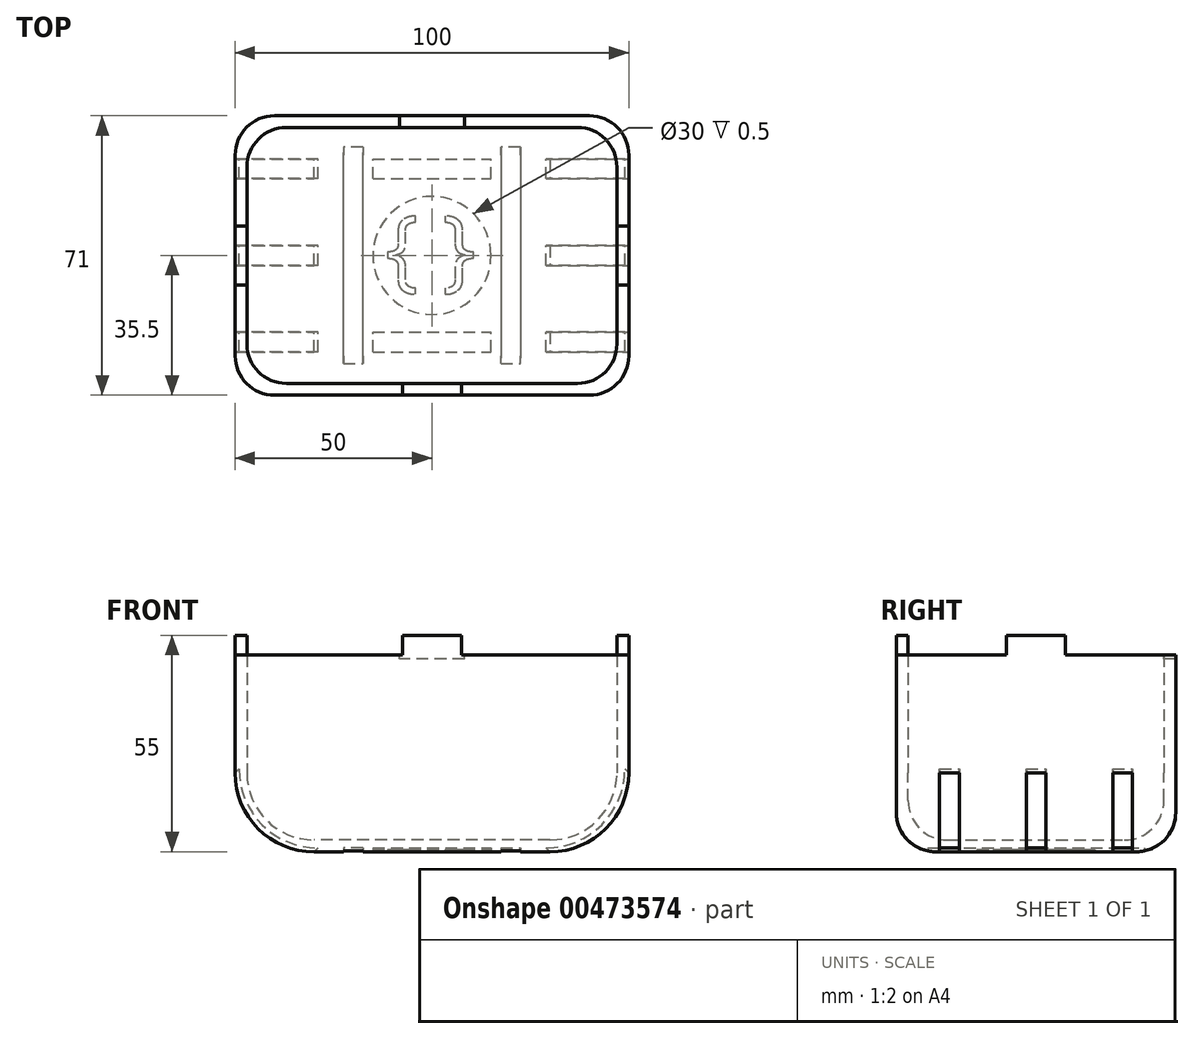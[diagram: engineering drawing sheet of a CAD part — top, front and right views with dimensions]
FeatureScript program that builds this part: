
annotation { "Feature Type Name" : "Feature", "Feature Type Description" : "" }
export const myFeature = defineFeature(function(context is Context, id is Id, definition is map)
    precondition{}
    {
        {
            var Q0;
            Q0=qCreatedBy(makeId("Top.planeOp"),FACE);
            var sketch = newSketch(context, id + "F0", { "sketchPlane" : qUnion([Q0])});
            skLineSegment(sketch, "E0.bottom", {"start": v(42.5, 28) * mm, "end": v(-42.5, 28) * mm});
            skLineSegment(sketch, "E0.top", {"start": v(42.5, -28) * mm, "end": v(-42.5, -28) * mm});
            skLineSegment(sketch, "E0.left", {"start": v(42.5, 28) * mm, "end": v(42.5, -28) * mm});
            skLineSegment(sketch, "E0.right", {"start": v(-42.5, 28) * mm, "end": v(-42.5, -28) * mm});
            skPoint(sketch, "E0.middle", {"position": v(0, 0) * mm});
            skLineSegment(sketch, "E1.bottom", {"start": v(50, 35.5) * mm, "end": v(-50, 35.5) * mm});
            skLineSegment(sketch, "E1.top", {"start": v(50, -35.5) * mm, "end": v(-50, -35.5) * mm});
            skLineSegment(sketch, "E1.left", {"start": v(50, 35.5) * mm, "end": v(50, -35.5) * mm});
            skLineSegment(sketch, "E1.right", {"start": v(-50, 35.5) * mm, "end": v(-50, -35.5) * mm});
            skSolve(sketch);
        }
        {
            var Q0;
            Q0=makeQuery(id+"F0.imprint","IMPRINT",FACE,{"disambiguationData":[TD([[makeQuery(id+"F0.imprint","IMPRINT",EDGE,{"derivedFrom":sQuery(id+"F0.wireOp",EDGE,"E0.bottom")}),-1.0]])]});
            var Q1;
            Q1=makeQuery(id+"F0.imprint","IMPRINT",FACE,{"disambiguationData":[TD([[makeQuery(id+"F0.imprint","IMPRINT",EDGE,{"derivedFrom":sQuery(id+"F0.wireOp",EDGE,"E0.bottom")}),1.0]])]});
            extrude(context, id + "F1", {"entities" : qUnion([Q0, Q1]), "depth" : 55 * mm});
        }
        {
            var Q0;
            Q0=makeQuery(id+"F1.opExtrude","CAP_EDGE",EDGE,{"disambiguationData":[OSD([sQuery(id+"F0.wireOp",EDGE,"E1.right")])],"isStart":true});
            var Q1;
            Q1=makeQuery(id+"F1.opExtrude","CAP_EDGE",EDGE,{"disambiguationData":[OSD([sQuery(id+"F0.wireOp",EDGE,"E1.left")])],"isStart":true});
            fillet(context, id + "F2", {"entities" : qUnion([Q0, Q1]), "radius" : 20 * mm, "tangentPropagation" : true, "allowEdgeOverflow" : false});
        }
        {
            var Q0;
            Q0=makeQuery(id+"F1.opExtrude","CAP_FACE",FACE,{"disambiguationData":[OSD([sQuery(id+"F0.wireOp",EDGE,"E1.bottom"),sQuery(id+"F0.wireOp",EDGE,"E1.top"),sQuery(id+"F0.wireOp",EDGE,"E1.left"),sQuery(id+"F0.wireOp",EDGE,"E1.right")])],"isStart":false});
            shell(context, id + "F3", {"entities" : qUnion([Q0]), "thickness" : 3 * mm});
        }
        {
            var Q0;
            Q0=makeQuery(id+"F1.opExtrude","SWEPT_FACE",FACE,{"disambiguationData":[OSD([sQuery(id+"F0.wireOp",EDGE,"E1.bottom")])]});
            var sketch = newSketch(context, id + "F4", { "sketchPlane" : qUnion([Q0])});
            skLineSegment(sketch, "E2.bottom", {"start": v(-50, 55) * mm, "end": v(50, 55) * mm});
            skLineSegment(sketch, "E2.top", {"start": v(-50, 0) * mm, "end": v(50, 0) * mm});
            skLineSegment(sketch, "E2.left", {"start": v(-50, 55) * mm, "end": v(-50, 0) * mm});
            skLineSegment(sketch, "E2.right", {"start": v(50, 55) * mm, "end": v(50, 0) * mm});
            skPoint(sketch, "E3", {"position": v(0, 27.5) * mm});
            skPoint(sketch, "E3.positionSnap0", {"position": v(-50, 27.5) * mm});
            skLineSegment(sketch, "E4.bottom", {"start": v(49, 54) * mm, "end": v(-49, 54) * mm});
            skLineSegment(sketch, "E4.top", {"start": v(29, 1) * mm, "end": v(-29, 1) * mm});
            skLineSegment(sketch, "E4.left", {"start": v(49, 54) * mm, "end": v(49, 21) * mm});
            skLineSegment(sketch, "E4.right", {"start": v(-49, 54) * mm, "end": v(-49, 21) * mm});
            skPoint(sketch, "E5.visualSharp", {"position": v(49, 1) * mm});
            skArc(sketch, "E5.filletArc", {"start": v(29, 1) * mm, "mid": v(43.14, 6.86) * mm, "end": v(49, 21) * mm});
            skPoint(sketch, "E6.visualSharp", {"position": v(-49, 1) * mm});
            skArc(sketch, "E6.filletArc", {"start": v(-49, 21) * mm, "mid": v(-43.14, 6.86) * mm, "end": v(-29, 1) * mm});
            skLineSegment(sketch, "E7", {"start": v(-29, 1) * mm, "end": v(-30, 0) * mm});
            skLineSegment(sketch, "E8", {"start": v(29, 1) * mm, "end": v(30, 0) * mm});
            skLineSegment(sketch, "E9", {"start": v(49, 21) * mm, "end": v(50, 20) * mm});
            skLineSegment(sketch, "E10", {"start": v(-49, 21) * mm, "end": v(-50, 20) * mm});
            skSolve(sketch);
        }
        {
            var Q0;
            Q0=makeQuery(id+"F4.imprint","IMPRINT",FACE,{"disambiguationData":[TD([[makeQuery(id+"F4.imprint","IMPRINT",EDGE,{"derivedFrom":sQuery(id+"F4.wireOp",EDGE,"E6.filletArc")}),-1.0]])]});
            var Q1;
            Q1=makeQuery(id+"F4.imprint","IMPRINT",FACE,{"disambiguationData":[TD([[makeQuery(id+"F4.imprint","IMPRINT",EDGE,{"derivedFrom":sQuery(id+"F4.wireOp",EDGE,"E5.filletArc")}),-1.0]])]});
            extrude(context, id + "F5", {"entities" : qUnion([Q0, Q1]), "operationType" : NewBodyOperationType.REMOVE, "oppositeDirection" : true, "depth" : 60 * mm});
        }
        {
            var Q0;
            Q0=makeQuery(id+"F4.imprint","IMPRINT",FACE,{"disambiguationData":[TD([[makeQuery(id+"F4.imprint","IMPRINT",EDGE,{"derivedFrom":sQuery(id+"F4.wireOp",EDGE,"E6.filletArc")}),-1.0]])]});
            var Q1;
            Q1=makeQuery(id+"F4.imprint","IMPRINT",FACE,{"disambiguationData":[TD([[makeQuery(id+"F4.imprint","IMPRINT",EDGE,{"derivedFrom":sQuery(id+"F4.wireOp",EDGE,"E5.filletArc")}),-1.0]])]});
            extrude(context, id + "F6", {"entities" : qUnion([Q0, Q1]), "operationType" : NewBodyOperationType.ADD, "oppositeDirection" : true, "depth" : 55 * mm});
        }
        {
            var Q0;
            Q0=makeQuery(id+"F4.imprint","IMPRINT",FACE,{"disambiguationData":[TD([[makeQuery(id+"F4.imprint","IMPRINT",EDGE,{"derivedFrom":sQuery(id+"F4.wireOp",EDGE,"E6.filletArc")}),-1.0]])]});
            var Q1;
            Q1=makeQuery(id+"F4.imprint","IMPRINT",FACE,{"disambiguationData":[TD([[makeQuery(id+"F4.imprint","IMPRINT",EDGE,{"derivedFrom":sQuery(id+"F4.wireOp",EDGE,"E5.filletArc")}),-1.0]])]});
            extrude(context, id + "F7", {"entities" : qUnion([Q0, Q1]), "operationType" : NewBodyOperationType.REMOVE, "oppositeDirection" : true, "depth" : 38 * mm});
        }
        {
            var Q0;
            Q0=makeQuery(id+"F4.imprint","IMPRINT",FACE,{"disambiguationData":[TD([[makeQuery(id+"F4.imprint","IMPRINT",EDGE,{"derivedFrom":sQuery(id+"F4.wireOp",EDGE,"E6.filletArc")}),-1.0]])]});
            var Q1;
            Q1=makeQuery(id+"F4.imprint","IMPRINT",FACE,{"disambiguationData":[TD([[makeQuery(id+"F4.imprint","IMPRINT",EDGE,{"derivedFrom":sQuery(id+"F4.wireOp",EDGE,"E5.filletArc")}),-1.0]])]});
            extrude(context, id + "F8", {"entities" : qUnion([Q0, Q1]), "operationType" : NewBodyOperationType.ADD, "oppositeDirection" : true, "depth" : 33 * mm});
        }
        {
            var Q0;
            Q0=makeQuery(id+"F4.imprint","IMPRINT",FACE,{"disambiguationData":[TD([[makeQuery(id+"F4.imprint","IMPRINT",EDGE,{"derivedFrom":sQuery(id+"F4.wireOp",EDGE,"E6.filletArc")}),-1.0]])]});
            var Q1;
            Q1=makeQuery(id+"F4.imprint","IMPRINT",FACE,{"disambiguationData":[TD([[makeQuery(id+"F4.imprint","IMPRINT",EDGE,{"derivedFrom":sQuery(id+"F4.wireOp",EDGE,"E5.filletArc")}),-1.0]])]});
            extrude(context, id + "F9", {"entities" : qUnion([Q0, Q1]), "operationType" : NewBodyOperationType.REMOVE, "oppositeDirection" : true, "depth" : 16 * mm});
        }
        {
            var Q0;
            Q0=makeQuery(id+"F4.imprint","IMPRINT",FACE,{"disambiguationData":[TD([[makeQuery(id+"F4.imprint","IMPRINT",EDGE,{"derivedFrom":sQuery(id+"F4.wireOp",EDGE,"E6.filletArc")}),-1.0]])]});
            var Q1;
            Q1=makeQuery(id+"F4.imprint","IMPRINT",FACE,{"disambiguationData":[TD([[makeQuery(id+"F4.imprint","IMPRINT",EDGE,{"derivedFrom":sQuery(id+"F4.wireOp",EDGE,"E5.filletArc")}),-1.0]])]});
            extrude(context, id + "F10", {"entities" : qUnion([Q0, Q1]), "operationType" : NewBodyOperationType.ADD, "oppositeDirection" : true, "depth" : 11 * mm});
        }
        {
            var Q0;
            Q0=makeQuery(id+"F1.opExtrude","CAP_FACE",FACE,{"disambiguationData":[OSD([sQuery(id+"F0.wireOp",EDGE,"E1.bottom"),sQuery(id+"F0.wireOp",EDGE,"E1.top"),sQuery(id+"F0.wireOp",EDGE,"E1.left"),sQuery(id+"F0.wireOp",EDGE,"E1.right")])],"isStart":true});
            var sketch = newSketch(context, id + "F11", { "sketchPlane" : qUnion([Q0])});
            skLineSegment(sketch, "E11.bottom", {"start": v(30, 35.5) * mm, "end": v(-30, 35.5) * mm});
            skLineSegment(sketch, "E11.top", {"start": v(30, -35.5) * mm, "end": v(-30, -35.5) * mm});
            skLineSegment(sketch, "E11.left", {"start": v(30, 35.5) * mm, "end": v(30, -35.5) * mm});
            skLineSegment(sketch, "E11.right", {"start": v(-30, 35.5) * mm, "end": v(-30, -35.5) * mm});
            skPoint(sketch, "E11.middle", {"position": v(0, 0) * mm});
            skLineSegment(sketch, "E12.bottom", {"start": v(-30, 24.5) * mm, "end": v(30, 24.5) * mm});
            skLineSegment(sketch, "E12.top", {"start": v(-30, 19.5) * mm, "end": v(30, 19.5) * mm});
            skLineSegment(sketch, "E12.left", {"start": v(-30, 24.5) * mm, "end": v(-30, 19.5) * mm});
            skLineSegment(sketch, "E12.right", {"start": v(30, 24.5) * mm, "end": v(30, 19.5) * mm});
            skLineSegment(sketch, "E13.bottom", {"start": v(-30, 2.5) * mm, "end": v(30, 2.5) * mm});
            skLineSegment(sketch, "E13.top", {"start": v(-30, -2.5) * mm, "end": v(30, -2.5) * mm});
            skLineSegment(sketch, "E13.left", {"start": v(-30, 2.5) * mm, "end": v(-30, -2.5) * mm});
            skLineSegment(sketch, "E13.right", {"start": v(30, 2.5) * mm, "end": v(30, -2.5) * mm});
            skLineSegment(sketch, "E14.bottom", {"start": v(-30, -19.5) * mm, "end": v(30, -19.5) * mm});
            skLineSegment(sketch, "E14.top", {"start": v(-30, -24.5) * mm, "end": v(30, -24.5) * mm});
            skLineSegment(sketch, "E14.left", {"start": v(-30, -19.5) * mm, "end": v(-30, -24.5) * mm});
            skLineSegment(sketch, "E14.right", {"start": v(30, -19.5) * mm, "end": v(30, -24.5) * mm});
            skLineSegment(sketch, "E15", {"start": v(-20, 2.5) * mm, "end": v(-20, -2.5) * mm});
            skLineSegment(sketch, "E16", {"start": v(20, 2.5) * mm, "end": v(20, -2.5) * mm});
            skLineSegment(sketch, "E17", {"start": v(-25, 24.5) * mm, "end": v(-25, 19.5) * mm});
            skLineSegment(sketch, "E18", {"start": v(25, 24.5) * mm, "end": v(25, 19.5) * mm});
            skLineSegment(sketch, "E19", {"start": v(-15, 24.5) * mm, "end": v(-15, 19.5) * mm});
            skLineSegment(sketch, "E20", {"start": v(15, 24.5) * mm, "end": v(15, 19.5) * mm});
            skLineSegment(sketch, "E21.0.1.0", {"start": v(25, -19.5) * mm, "end": v(25, -24.5) * mm});
            skLineSegment(sketch, "E21.0.1.1", {"start": v(-25, -19.5) * mm, "end": v(-25, -24.5) * mm});
            skLineSegment(sketch, "E21.0.1.2", {"start": v(-15, -19.5) * mm, "end": v(-15, -24.5) * mm});
            skLineSegment(sketch, "E21.0.1.3", {"start": v(15, -19.5) * mm, "end": v(15, -24.5) * mm});
            skLineSegment(sketch, "E21.direction1", {"start": v(-25, 19.5) * mm, "end": v(0, 19.5) * mm, "construction": true});
            skLineSegment(sketch, "E21.direction2", {"start": v(-25, 19.5) * mm, "end": v(-25, -24.5) * mm, "construction": true});
            skLineSegment(sketch, "E22.bottom", {"start": v(-17.5, -2.5) * mm, "end": v(-22.5, -2.5) * mm});
            skLineSegment(sketch, "E22.top", {"start": v(-17.5, 27.5) * mm, "end": v(-22.5, 27.5) * mm});
            skLineSegment(sketch, "E22.left", {"start": v(-17.5, -2.5) * mm, "end": v(-17.5, 27.5) * mm});
            skLineSegment(sketch, "E22.right", {"start": v(-22.5, -2.5) * mm, "end": v(-22.5, 27.5) * mm});
            skLineSegment(sketch, "E23.1.0.0", {"start": v(17.5, -2.5) * mm, "end": v(17.5, 27.5) * mm});
            skLineSegment(sketch, "E23.1.0.1", {"start": v(22.5, 27.5) * mm, "end": v(17.5, 27.5) * mm});
            skLineSegment(sketch, "E23.1.0.2", {"start": v(22.5, -2.5) * mm, "end": v(17.5, -2.5) * mm});
            skLineSegment(sketch, "E23.1.0.3", {"start": v(22.5, -2.5) * mm, "end": v(22.5, 27.5) * mm});
            skLineSegment(sketch, "E23.direction1", {"start": v(-17.5, -2.5) * mm, "end": v(22.5, -2.5) * mm, "construction": true});
            skLineSegment(sketch, "E24.bottom", {"start": v(-22.5, 2.5) * mm, "end": v(-17.5, 2.5) * mm});
            skLineSegment(sketch, "E24.top", {"start": v(-22.5, -27.5) * mm, "end": v(-17.5, -27.5) * mm});
            skLineSegment(sketch, "E24.left", {"start": v(-22.5, 2.5) * mm, "end": v(-22.5, -27.5) * mm});
            skLineSegment(sketch, "E24.right", {"start": v(-17.5, 2.5) * mm, "end": v(-17.5, -27.5) * mm});
            skLineSegment(sketch, "E25.1.0.0", {"start": v(17.5, 2.5) * mm, "end": v(17.5, -27.5) * mm});
            skLineSegment(sketch, "E25.1.0.1", {"start": v(22.5, 2.5) * mm, "end": v(22.5, -27.5) * mm});
            skLineSegment(sketch, "E25.1.0.2", {"start": v(17.5, 2.5) * mm, "end": v(22.5, 2.5) * mm});
            skLineSegment(sketch, "E25.1.0.3", {"start": v(17.5, -27.5) * mm, "end": v(22.5, -27.5) * mm});
            skLineSegment(sketch, "E25.direction1", {"start": v(-17.5, -27.5) * mm, "end": v(22.5, -27.5) * mm, "construction": true});
            skSolve(sketch);
        }
        {
            var Q0;
            {var subQ0=sQuery(id+"F11.wireOp",EDGE,"E12.left");Q0=makeQuery(id+"F11.imprint","IMPRINT",FACE,{"disambiguationData":[TD([[makeQuery(id+"F11.imprint","IMPRINT",EDGE,{"derivedFrom":subQ0}),1.0]])]});}
            var Q1;
            {var subQ0=sQuery(id+"F11.wireOp",EDGE,"E12.right");Q1=makeQuery(id+"F11.imprint","IMPRINT",FACE,{"disambiguationData":[TD([[makeQuery(id+"F11.imprint","IMPRINT",EDGE,{"derivedFrom":subQ0}),1.0]])]});}
            var Q2;
            {var subQ0=sQuery(id+"F11.wireOp",EDGE,"E13.right");Q2=makeQuery(id+"F11.imprint","IMPRINT",FACE,{"disambiguationData":[TD([[makeQuery(id+"F11.imprint","IMPRINT",EDGE,{"derivedFrom":subQ0}),1.0]])]});}
            var Q3;
            {var subQ0=sQuery(id+"F11.wireOp",EDGE,"E19");Q3=makeQuery(id+"F11.imprint","IMPRINT",FACE,{"disambiguationData":[TD([[makeQuery(id+"F11.imprint","IMPRINT",EDGE,{"derivedFrom":subQ0}),1.0]])]});}
            var Q4;
            {var subQ0=sQuery(id+"F11.wireOp",EDGE,"E13.left");Q4=makeQuery(id+"F11.imprint","IMPRINT",FACE,{"disambiguationData":[TD([[makeQuery(id+"F11.imprint","IMPRINT",EDGE,{"derivedFrom":subQ0}),1.0]])]});}
            var Q5;
            {var subQ0=sQuery(id+"F11.wireOp",EDGE,"E14.left");Q5=makeQuery(id+"F11.imprint","IMPRINT",FACE,{"disambiguationData":[TD([[makeQuery(id+"F11.imprint","IMPRINT",EDGE,{"derivedFrom":subQ0}),1.0]])]});}
            var Q6;
            {var subQ0=sQuery(id+"F11.wireOp",EDGE,"E21.0.1.2");Q6=makeQuery(id+"F11.imprint","IMPRINT",FACE,{"disambiguationData":[TD([[makeQuery(id+"F11.imprint","IMPRINT",EDGE,{"derivedFrom":subQ0}),1.0]])]});}
            var Q7;
            {var subQ0=sQuery(id+"F11.wireOp",EDGE,"E14.right");Q7=makeQuery(id+"F11.imprint","IMPRINT",FACE,{"disambiguationData":[TD([[makeQuery(id+"F11.imprint","IMPRINT",EDGE,{"derivedFrom":subQ0}),1.0]])]});}
            var Q8;
            {var subQ0=sQuery(id+"F11.wireOp",EDGE,"E24.left");var subQ1=sQuery(id+"F11.wireOp",EDGE,"E14.bottom");var subQ2=makeQuery(id+"F11.imprint","INTERSECT",VERTEX,{"derivedFrom":[subQ1,subQ0]});Q8=makeQuery(id+"F11.imprint","IMPRINT",FACE,{"disambiguationData":[TD([[makeQuery(id+"F11.imprint","IMPRINT",EDGE,{"disambiguationData":[TD([[subQ2,-1.0]])],"derivedFrom":subQ1}),-1.0]])]});}
            var Q9;
            {var subQ5=sQuery(id+"F11.wireOp",EDGE,"E24.top");Q9=makeQuery(id+"F11.imprint","IMPRINT",FACE,{"disambiguationData":[TD([[makeQuery(id+"F11.imprint","IMPRINT",EDGE,{"derivedFrom":subQ5}),1.0]])]});}
            var Q10;
            {var subQ2=sQuery(id+"F11.wireOp",EDGE,"E24.left");var subQ7=sQuery(id+"F11.wireOp",EDGE,"E14.bottom");var subQ8=makeQuery(id+"F11.imprint","INTERSECT",VERTEX,{"derivedFrom":[subQ7,subQ2]});Q10=makeQuery(id+"F11.imprint","IMPRINT",FACE,{"disambiguationData":[TD([[makeQuery(id+"F11.imprint","IMPRINT",EDGE,{"disambiguationData":[TD([[subQ8,-1.0]])],"derivedFrom":subQ7}),1.0]])]});}
            var Q11;
            {var subQ0=sQuery(id+"F11.wireOp",EDGE,"E15");Q11=makeQuery(id+"F11.imprint","IMPRINT",FACE,{"disambiguationData":[TD([[makeQuery(id+"F11.imprint","IMPRINT",EDGE,{"derivedFrom":subQ0}),1.0]])]});}
            var Q12;
            {var subQ0=sQuery(id+"F11.wireOp",EDGE,"E15");Q12=makeQuery(id+"F11.imprint","IMPRINT",FACE,{"disambiguationData":[TD([[makeQuery(id+"F11.imprint","IMPRINT",EDGE,{"derivedFrom":subQ0}),-1.0]])]});}
            var Q13;
            {var subQ1=sQuery(id+"F11.wireOp",EDGE,"E22.right");var subQ4=sQuery(id+"F11.wireOp",EDGE,"E12.top");var subQ5=makeQuery(id+"F11.imprint","INTERSECT",VERTEX,{"derivedFrom":[subQ4,subQ1]});Q13=makeQuery(id+"F11.imprint","IMPRINT",FACE,{"disambiguationData":[TD([[makeQuery(id+"F11.imprint","IMPRINT",EDGE,{"disambiguationData":[TD([[subQ5,-1.0]])],"derivedFrom":subQ4}),-1.0]])]});}
            var Q14;
            {var subQ0=sQuery(id+"F11.wireOp",EDGE,"E22.right");var subQ1=sQuery(id+"F11.wireOp",EDGE,"E12.bottom");var subQ2=makeQuery(id+"F11.imprint","INTERSECT",VERTEX,{"derivedFrom":[subQ1,subQ0]});Q14=makeQuery(id+"F11.imprint","IMPRINT",FACE,{"disambiguationData":[TD([[makeQuery(id+"F11.imprint","IMPRINT",EDGE,{"disambiguationData":[TD([[subQ2,-1.0]])],"derivedFrom":subQ1}),-1.0]])]});}
            var Q15;
            {var subQ5=sQuery(id+"F11.wireOp",EDGE,"E22.top");Q15=makeQuery(id+"F11.imprint","IMPRINT",FACE,{"disambiguationData":[TD([[makeQuery(id+"F11.imprint","IMPRINT",EDGE,{"derivedFrom":subQ5}),1.0]])]});}
            var Q16;
            {var subQ5=sQuery(id+"F11.wireOp",EDGE,"E23.1.0.1");Q16=makeQuery(id+"F11.imprint","IMPRINT",FACE,{"disambiguationData":[TD([[makeQuery(id+"F11.imprint","IMPRINT",EDGE,{"derivedFrom":subQ5}),1.0]])]});}
            var Q17;
            {var subQ0=sQuery(id+"F11.wireOp",EDGE,"E23.1.0.0");var subQ1=sQuery(id+"F11.wireOp",EDGE,"E12.bottom");var subQ2=makeQuery(id+"F11.imprint","INTERSECT",VERTEX,{"derivedFrom":[subQ1,subQ0]});Q17=makeQuery(id+"F11.imprint","IMPRINT",FACE,{"disambiguationData":[TD([[makeQuery(id+"F11.imprint","IMPRINT",EDGE,{"disambiguationData":[TD([[subQ2,-1.0]])],"derivedFrom":subQ1}),-1.0]])]});}
            var Q18;
            {var subQ4=sQuery(id+"F11.wireOp",EDGE,"E12.top");var subQ7=sQuery(id+"F11.wireOp",EDGE,"E23.1.0.0");var subQ9=makeQuery(id+"F11.imprint","INTERSECT",VERTEX,{"derivedFrom":[subQ4,subQ7]});Q18=makeQuery(id+"F11.imprint","IMPRINT",FACE,{"disambiguationData":[TD([[makeQuery(id+"F11.imprint","IMPRINT",EDGE,{"disambiguationData":[TD([[subQ9,-1.0]])],"derivedFrom":subQ4}),-1.0]])]});}
            var Q19;
            {var subQ0=sQuery(id+"F11.wireOp",EDGE,"E16");Q19=makeQuery(id+"F11.imprint","IMPRINT",FACE,{"disambiguationData":[TD([[makeQuery(id+"F11.imprint","IMPRINT",EDGE,{"derivedFrom":subQ0}),1.0]])]});}
            var Q20;
            {var subQ0=sQuery(id+"F11.wireOp",EDGE,"E16");Q20=makeQuery(id+"F11.imprint","IMPRINT",FACE,{"disambiguationData":[TD([[makeQuery(id+"F11.imprint","IMPRINT",EDGE,{"derivedFrom":subQ0}),-1.0]])]});}
            var Q21;
            {var subQ0=sQuery(id+"F11.wireOp",EDGE,"E25.1.0.0");var subQ4=sQuery(id+"F11.wireOp",EDGE,"E14.bottom");var subQ5=makeQuery(id+"F11.imprint","INTERSECT",VERTEX,{"derivedFrom":[subQ4,subQ0]});Q21=makeQuery(id+"F11.imprint","IMPRINT",FACE,{"disambiguationData":[TD([[makeQuery(id+"F11.imprint","IMPRINT",EDGE,{"disambiguationData":[TD([[subQ5,-1.0]])],"derivedFrom":subQ4}),1.0]])]});}
            var Q22;
            {var subQ0=sQuery(id+"F11.wireOp",EDGE,"E25.1.0.0");var subQ1=sQuery(id+"F11.wireOp",EDGE,"E14.bottom");var subQ2=makeQuery(id+"F11.imprint","INTERSECT",VERTEX,{"derivedFrom":[subQ1,subQ0]});Q22=makeQuery(id+"F11.imprint","IMPRINT",FACE,{"disambiguationData":[TD([[makeQuery(id+"F11.imprint","IMPRINT",EDGE,{"disambiguationData":[TD([[subQ2,-1.0]])],"derivedFrom":subQ1}),-1.0]])]});}
            var Q23;
            {var subQ5=sQuery(id+"F11.wireOp",EDGE,"E25.1.0.3");Q23=makeQuery(id+"F11.imprint","IMPRINT",FACE,{"disambiguationData":[TD([[makeQuery(id+"F11.imprint","IMPRINT",EDGE,{"derivedFrom":subQ5}),1.0]])]});}
            extrude(context, id + "F12", {"entities" : qUnion([Q0, Q1, Q2, Q3, Q4, Q5, Q6, Q7, Q8, Q9, Q10, Q11, Q12, Q13, Q14, Q15, Q16, Q17, Q18, Q19, Q20, Q21, Q22, Q23]), "operationType" : NewBodyOperationType.REMOVE, "oppositeDirection" : true, "depth" : 1 * mm});
        }
        {
            var Q0;
            Q0=makeQuery(id+"F1.opExtrude","CAP_FACE",FACE,{"disambiguationData":[OSD([sQuery(id+"F0.wireOp",EDGE,"E1.bottom"),sQuery(id+"F0.wireOp",EDGE,"E1.top"),sQuery(id+"F0.wireOp",EDGE,"E1.left"),sQuery(id+"F0.wireOp",EDGE,"E1.right")])],"isStart":true});
            var sketch = newSketch(context, id + "F13", { "sketchPlane" : qUnion([Q0])});
            skCircle(sketch, "E26", {"center": v(0, 0) * mm, "radius": 15 * mm});
            skText(sketch, "E27", { "text": "{ }", "fontName": "OpenSans-Regular.ttf"});
            const initialGuessF13  = {"E27": [-0.012, -0.00642, 1, 0, 0.01642]};
            skSetInitialGuess(sketch, initialGuessF13);
            skSolve(sketch);
        }
        {
            var Q0;
            Q0=makeQuery(id+"F13.imprint","IMPRINT",FACE,{"disambiguationData":[TD([[makeQuery(id+"F13.imprint","IMPRINT",EDGE,{"derivedFrom":sQuery(id+"F13.wireOp",EDGE,"E26")}),1.0]])]});
            extrude(context, id + "F14", {"entities" : qUnion([Q0]), "operationType" : NewBodyOperationType.REMOVE, "oppositeDirection" : true, "depth" : .5 * mm});
        }
        {
            var Q0;
            Q0=makeQuery(id+"F1.opExtrude","CAP_FACE",FACE,{"disambiguationData":[OSD([sQuery(id+"F0.wireOp",EDGE,"E1.bottom"),sQuery(id+"F0.wireOp",EDGE,"E1.top"),sQuery(id+"F0.wireOp",EDGE,"E1.left"),sQuery(id+"F0.wireOp",EDGE,"E1.right")])],"isStart":false});
            var sketch = newSketch(context, id + "F15", { "sketchPlane" : qUnion([Q0])});
            skLineSegment(sketch, "E28.bottom", {"start": v(7.5, 35.5) * mm, "end": v(-7.5, 35.5) * mm});
            skLineSegment(sketch, "E28.top", {"start": v(7.5, -35.5) * mm, "end": v(-7.5, -35.5) * mm});
            skLineSegment(sketch, "E28.left", {"start": v(7.5, 35.5) * mm, "end": v(7.5, -35.5) * mm});
            skLineSegment(sketch, "E28.right", {"start": v(-7.5, 35.5) * mm, "end": v(-7.5, -35.5) * mm});
            skPoint(sketch, "E28.middle", {"position": v(0, 0) * mm});
            skLineSegment(sketch, "E29.bottom", {"start": v(50, 7.5) * mm, "end": v(-50, 7.5) * mm});
            skLineSegment(sketch, "E29.top", {"start": v(50, -7.5) * mm, "end": v(-50, -7.5) * mm});
            skLineSegment(sketch, "E29.left", {"start": v(50, 7.5) * mm, "end": v(50, -7.5) * mm});
            skLineSegment(sketch, "E29.right", {"start": v(-50, 7.5) * mm, "end": v(-50, -7.5) * mm});
            skSolve(sketch);
        }
        {
            var Q0;
            {var subQ0=sQuery(id+"F0.wireOp",EDGE,"E1.left");var subQ1=makeQuery(id+"F1.opExtrude","CAP_EDGE",EDGE,{"disambiguationData":[OSD([subQ0])],"isStart":false});var subQ2=sQuery(id+"F0.wireOp",EDGE,"E1.bottom");var subQ3=makeQuery(id+"F1.opExtrude","CAP_EDGE",EDGE,{"disambiguationData":[OSD([subQ2])],"isStart":false});var subQ4=makeQuery(id+"F15.imprint","INTERSECT",VERTEX,{"derivedFrom":[subQ3,subQ1]});Q0=makeQuery(id+"F15.imprint","IMPRINT",FACE,{"disambiguationData":[TD([[makeQuery(id+"F15.imprint","IMPRINT",EDGE,{"disambiguationData":[TD([[subQ4,-1.0]])],"derivedFrom":subQ3}),1.0]])]});}
            var Q1;
            {var subQ0=sQuery(id+"F0.wireOp",EDGE,"E1.right");var subQ1=makeQuery(id+"F1.opExtrude","CAP_EDGE",EDGE,{"disambiguationData":[OSD([subQ0])],"isStart":false});var subQ2=sQuery(id+"F0.wireOp",EDGE,"E1.bottom");var subQ3=makeQuery(id+"F1.opExtrude","CAP_EDGE",EDGE,{"disambiguationData":[OSD([subQ2])],"isStart":false});var subQ4=makeQuery(id+"F15.imprint","INTERSECT",VERTEX,{"derivedFrom":[subQ3,subQ1]});Q1=makeQuery(id+"F15.imprint","IMPRINT",FACE,{"disambiguationData":[TD([[makeQuery(id+"F15.imprint","IMPRINT",EDGE,{"disambiguationData":[TD([[subQ4,1.0]])],"derivedFrom":subQ3}),1.0]])]});}
            var Q2;
            {var subQ0=sQuery(id+"F0.wireOp",EDGE,"E1.right");var subQ1=makeQuery(id+"F1.opExtrude","CAP_EDGE",EDGE,{"disambiguationData":[OSD([subQ0])],"isStart":false});var subQ2=sQuery(id+"F0.wireOp",EDGE,"E1.top");var subQ3=makeQuery(id+"F1.opExtrude","CAP_EDGE",EDGE,{"disambiguationData":[OSD([subQ2])],"isStart":false});var subQ4=makeQuery(id+"F15.imprint","INTERSECT",VERTEX,{"derivedFrom":[subQ3,subQ1]});Q2=makeQuery(id+"F15.imprint","IMPRINT",FACE,{"disambiguationData":[TD([[makeQuery(id+"F15.imprint","IMPRINT",EDGE,{"disambiguationData":[TD([[subQ4,1.0]])],"derivedFrom":subQ3}),-1.0]])]});}
            var Q3;
            {var subQ0=sQuery(id+"F0.wireOp",EDGE,"E1.left");var subQ1=makeQuery(id+"F1.opExtrude","CAP_EDGE",EDGE,{"disambiguationData":[OSD([subQ0])],"isStart":false});var subQ2=sQuery(id+"F0.wireOp",EDGE,"E1.top");var subQ3=makeQuery(id+"F1.opExtrude","CAP_EDGE",EDGE,{"disambiguationData":[OSD([subQ2])],"isStart":false});var subQ4=makeQuery(id+"F15.imprint","INTERSECT",VERTEX,{"derivedFrom":[subQ3,subQ1]});Q3=makeQuery(id+"F15.imprint","IMPRINT",FACE,{"disambiguationData":[TD([[makeQuery(id+"F15.imprint","IMPRINT",EDGE,{"disambiguationData":[TD([[subQ4,-1.0]])],"derivedFrom":subQ3}),-1.0]])]});}
            var Q4;
            {var subQ0=sQuery(id+"F15.wireOp",EDGE,"E28.bottom");Q4=makeQuery(id+"F15.imprint","IMPRINT",FACE,{"disambiguationData":[TD([[makeQuery(id+"F15.imprint","IMPRINT",EDGE,{"derivedFrom":subQ0}),1.0]])]});}
            extrude(context, id + "F16", {"entities" : qUnion([Q0, Q1, Q2, Q3, Q4]), "operationType" : NewBodyOperationType.REMOVE, "oppositeDirection" : true, "depth" : 5 * mm});
        }
        {
            var Q0;
            Q0=makeQuery(id+"F16.boolean.opBoolean","COPY",FACE,{"derivedFrom":makeQuery(id+"F16.opExtrude","CAP_FACE",FACE,{"disambiguationData":[OSD([sQuery(id+"F0.wireOp",EDGE,"E1.bottom"),sQuery(id+"F0.wireOp",EDGE,"E1.left"),sQuery(id+"F0.wireOp",EDGE,"E1.right"),sQuery(id+"F15.wireOp",EDGE,"E28.bottom"),sQuery(id+"F15.wireOp",EDGE,"E29.bottom")])],"isStart":false})});
            var sketch = newSketch(context, id + "F17", { "sketchPlane" : qUnion([Q0])});
            skPoint(sketch, "E30", {"position": v(0, 32.5) * mm});
            skPoint(sketch, "E31", {"position": v(0, 35.5) * mm});
            skPoint(sketch, "E32", {"position": v(0, 34) * mm});
            skLineSegment(sketch, "E33.bottom", {"start": v(8.25, 35.5) * mm, "end": v(-8.25, 35.5) * mm});
            skLineSegment(sketch, "E33.top", {"start": v(8.25, 32.5) * mm, "end": v(-8.25, 32.5) * mm});
            skLineSegment(sketch, "E33.left", {"start": v(8.25, 35.5) * mm, "end": v(8.25, 32.5) * mm});
            skLineSegment(sketch, "E33.right", {"start": v(-8.25, 35.5) * mm, "end": v(-8.25, 32.5) * mm});
            skSolve(sketch);
        }
        {
            var Q0;
            Q0=makeQuery(id+"F17.imprint","IMPRINT",FACE,{"disambiguationData":[TD([[makeQuery(id+"F17.imprint","IMPRINT",EDGE,{"derivedFrom":sQuery(id+"F17.wireOp",EDGE,"E33.bottom")}),1.0]])]});
            extrude(context, id + "F18", {"entities" : qUnion([Q0]), "operationType" : NewBodyOperationType.REMOVE, "oppositeDirection" : true, "depth" : 1 * mm});
        }
        {
            var Q0;
            Q0=makeQuery(id+"F1.opExtrude","CAP_EDGE",EDGE,{"disambiguationData":[OSD([sQuery(id+"F0.wireOp",EDGE,"E1.bottom")])],"isStart":true});
            var Q1;
            Q1=makeQuery(id+"F1.opExtrude","CAP_EDGE",EDGE,{"disambiguationData":[OSD([sQuery(id+"F0.wireOp",EDGE,"E1.top")])],"isStart":true});
            var Q2;
            {var subQ0=sQuery(id+"F0.wireOp",EDGE,"E1.top");Q2=makeQuery(id+"F3.opShell","OFFSET_EDGE",EDGE,{"disambiguationData":[OSD([subQ0]),TDD([makeQuery(id+"F1.opExtrude","CAP_EDGE",EDGE,{"disambiguationData":[OSD([subQ0])],"isStart":true})])]});}
            var Q3;
            {var subQ0=sQuery(id+"F0.wireOp",EDGE,"E1.bottom");Q3=makeQuery(id+"F3.opShell","OFFSET_EDGE",EDGE,{"disambiguationData":[OSD([subQ0]),TDD([makeQuery(id+"F1.opExtrude","CAP_EDGE",EDGE,{"disambiguationData":[OSD([subQ0])],"isStart":true})])]});}
            fillet(context, id + "F19", {"entities" : qUnion([Q0, Q1, Q2, Q3]), "radius" : 10 * mm, "tangentPropagation" : true, "allowEdgeOverflow" : false});
        }
    });
